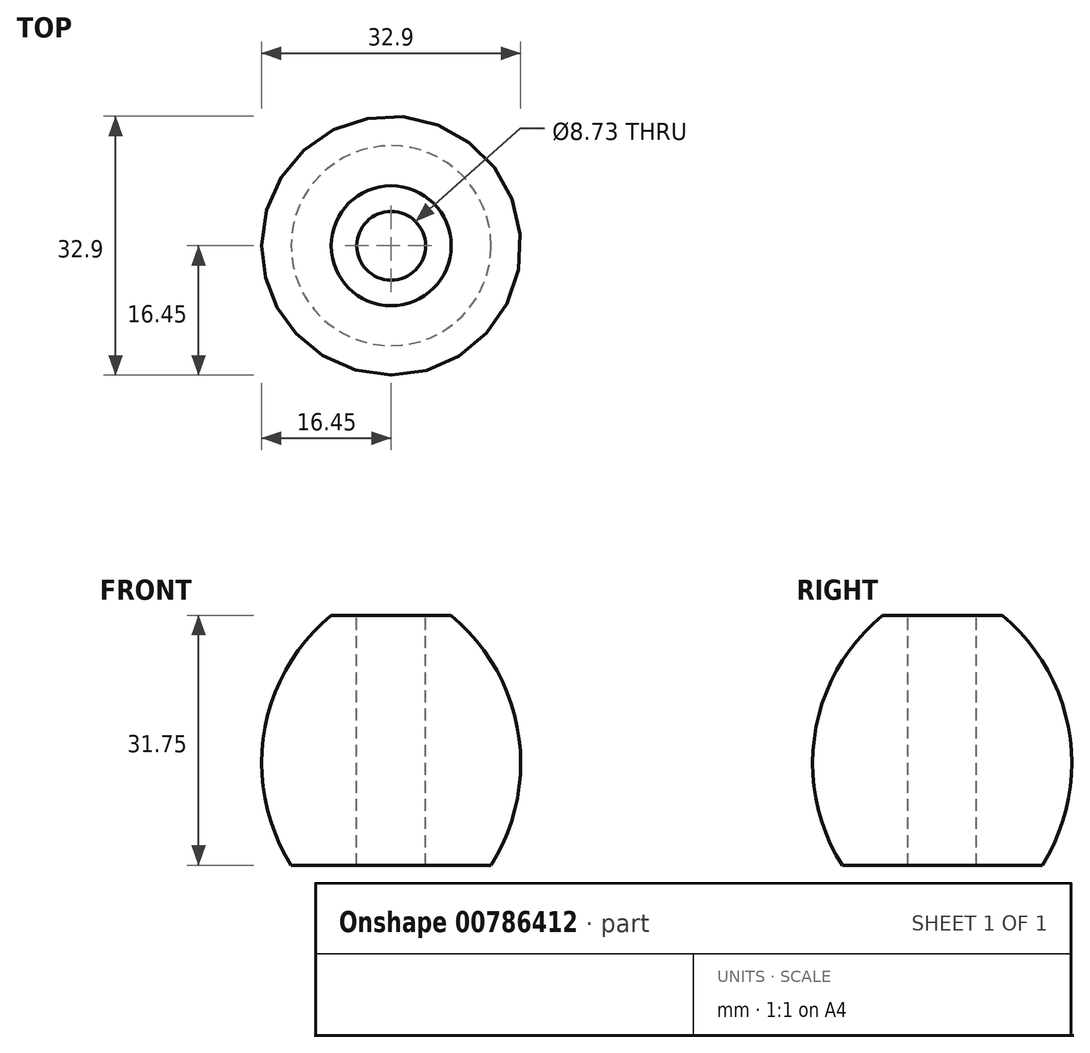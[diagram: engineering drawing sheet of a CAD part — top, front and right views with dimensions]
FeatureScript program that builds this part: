
annotation { "Feature Type Name" : "Feature", "Feature Type Description" : "" }
export const myFeature = defineFeature(function(context is Context, id is Id, definition is map)
    precondition{}
    {
        {
            var Q0;
            Q0=qCreatedBy(makeId("Front.planeOp"),FACE);
            var sketch = newSketch(context, id + "F0", { "sketchPlane" : qUnion([Q0])});
            skLineSegment(sketch, "E0", {"start": v(0, 0) * mm, "end": v(0, 31.75) * mm});
            skLineSegment(sketch, "E1", {"start": v(0, 0) * mm, "end": v(12.7, 0) * mm});
            skLineSegment(sketch, "E2", {"start": v(0, 31.75) * mm, "end": v(7.62, 31.75) * mm});
            skArc(sketch, "E3", {"start": v(12.7, 0) * mm, "mid": v(16.15, 16.83) * mm, "end": v(7.62, 31.75) * mm});
            skSolve(sketch);
        }
        {
            var Q0;
            Q0=makeQuery(id+"F0.imprint","IMPRINT",FACE,{"disambiguationData":[TD([[makeQuery(id+"F0.imprint","IMPRINT",EDGE,{"derivedFrom":sQuery(id+"F0.wireOp",EDGE,"E0")}),-1.0]])]});
            var Q1;
            Q1=sQuery(id+"F0.wireOp",EDGE,"E0");
            revolve(context, id + "F1", {"surfaceOperationType" : NewSurfaceOperationType.NEW, "entities" : qUnion([Q0]), "axis" : qUnion([Q1]), "revolveType" : RevolveType.FULL});
        }
        {
            var Q0;
            Q0=makeQuery(id+"F1.opRevolve","SWEPT_FACE",FACE,{"disambiguationData":[OSD([sQuery(id+"F0.wireOp",EDGE,"E2")])]});
            var sketch = newSketch(context, id + "F2", { "sketchPlane" : qUnion([Q0])});
            skCircle(sketch, "E4", {"center": v(0, 0) * mm, "radius": 4.37 * mm});
            skSolve(sketch);
        }
        {
            var Q0;
            Q0=makeQuery(id+"F2.imprint","IMPRINT",FACE,{"disambiguationData":[TD([[makeQuery(id+"F2.imprint","IMPRINT",EDGE,{"derivedFrom":sQuery(id+"F2.wireOp",EDGE,"E4")}),1.0]])]});
            extrude(context, id + "F3", {"entities" : qUnion([Q0]), "operationType" : NewBodyOperationType.REMOVE, "oppositeDirection" : true, "depth" : 25.4 * mm, "offsetDistance" : 25.4 * mm});
        }
        {
            var Q0;
            Q0=makeQuery(id+"F3.boolean.opBoolean","COPY",FACE,{"derivedFrom":makeQuery(id+"F3.opExtrude","CAP_FACE",FACE,{"disambiguationData":[OSD([sQuery(id+"F2.wireOp",EDGE,"E4")])],"isStart":false})});
            extrude(context, id + "F4", {"entities" : qUnion([Q0]), "operationType" : NewBodyOperationType.REMOVE, "oppositeDirection" : true, "depth" : 25.4 * mm, "offsetDistance" : 25.4 * mm});
        }
    });
